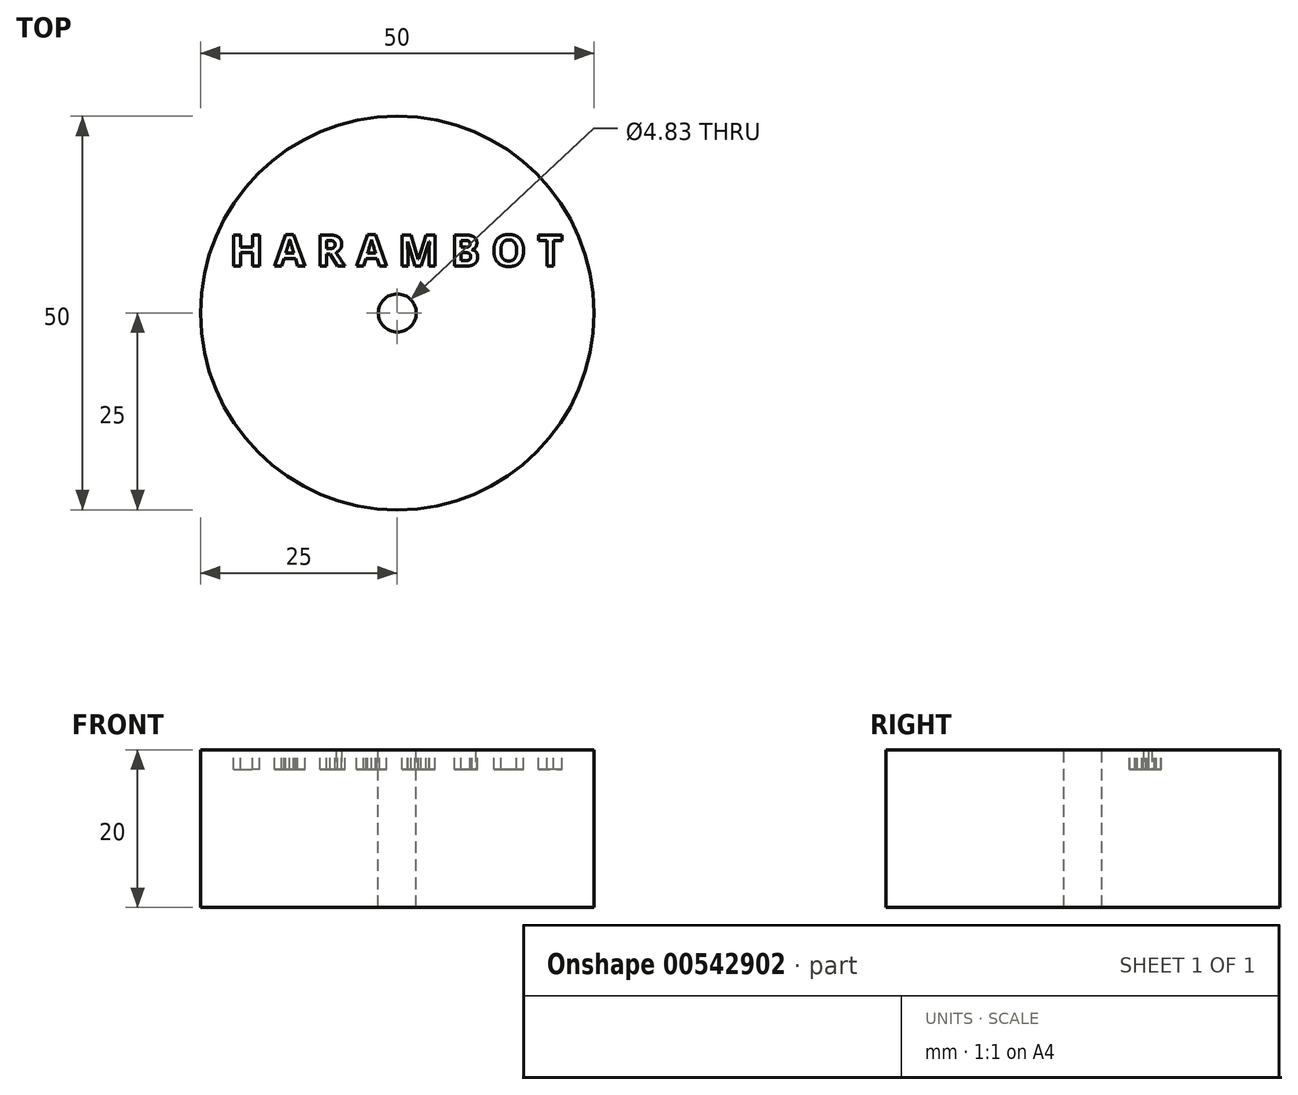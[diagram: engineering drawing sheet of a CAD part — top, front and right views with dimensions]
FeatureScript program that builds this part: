
annotation { "Feature Type Name" : "Feature", "Feature Type Description" : "" }
export const myFeature = defineFeature(function(context is Context, id is Id, definition is map)
    precondition{}
    {
        {
            var Q0;
            Q0=qCreatedBy(makeId("Top.planeOp"),FACE);
            var sketch = newSketch(context, id + "F0", { "sketchPlane" : qUnion([Q0])});
            skCircle(sketch, "E0", {"center": v(0, 0) * mm, "radius": 25 * mm});
            skSolve(sketch);
        }
        {
            var Q0;
            Q0 = qSketchRegion(id + "F0", true);
            extrude(context, id + "F1", {"entities" : qUnion([Q0]), "depth" : 20 * mm, "offsetDistance" : 25 * mm});
        }
        {
            var Q0;
            Q0=makeQuery(id+"F1.opExtrude","CAP_FACE",FACE,{"disambiguationData":[OSD([sQuery(id+"F0.wireOp",EDGE,"E0")])],"isStart":false});
            var sketch = newSketch(context, id + "F2", { "sketchPlane" : qUnion([Q0])});
            skCircle(sketch, "E1", {"center": v(0, 0) * mm, "radius": 2.41 * mm});
            skSolve(sketch);
        }
        {
            var Q0;
            Q0=makeQuery(id+"F2.imprint","IMPRINT",FACE,{"disambiguationData":[TD([[makeQuery(id+"F2.imprint","IMPRINT",EDGE,{"derivedFrom":sQuery(id+"F2.wireOp",EDGE,"E1")}),-1.0]])]});
            var sketch = newSketch(context, id + "F3", { "sketchPlane" : qUnion([Q0])});
            skText(sketch, "E2", { "text": "H A R A M B O T", "fontName": "OpenSans-Bold.ttf"});
            const initialGuessF3  = {"E2": [-0.02127, 0.00595, 1, 0, 0.004]};
            skSetInitialGuess(sketch, initialGuessF3);
            skSolve(sketch);
        }
        {
            var Q0;
            Q0 = qSketchRegion(id + "F3", true);
            extrude(context, id + "F4", {"entities" : qUnion([Q0]), "operationType" : NewBodyOperationType.REMOVE, "oppositeDirection" : true, "depth" : 2.5 * mm, "offsetDistance" : 25 * mm});
        }
        {
            var Q0;
            Q0 = qSketchRegion(id + "F2", true);
            extrude(context, id + "F5", {"entities" : qUnion([Q0]), "operationType" : NewBodyOperationType.REMOVE, "endBound" : BoundingType.THROUGH_ALL, "oppositeDirection" : true, "depth" : 25 * mm, "offsetDistance" : 25 * mm});
        }
    });
